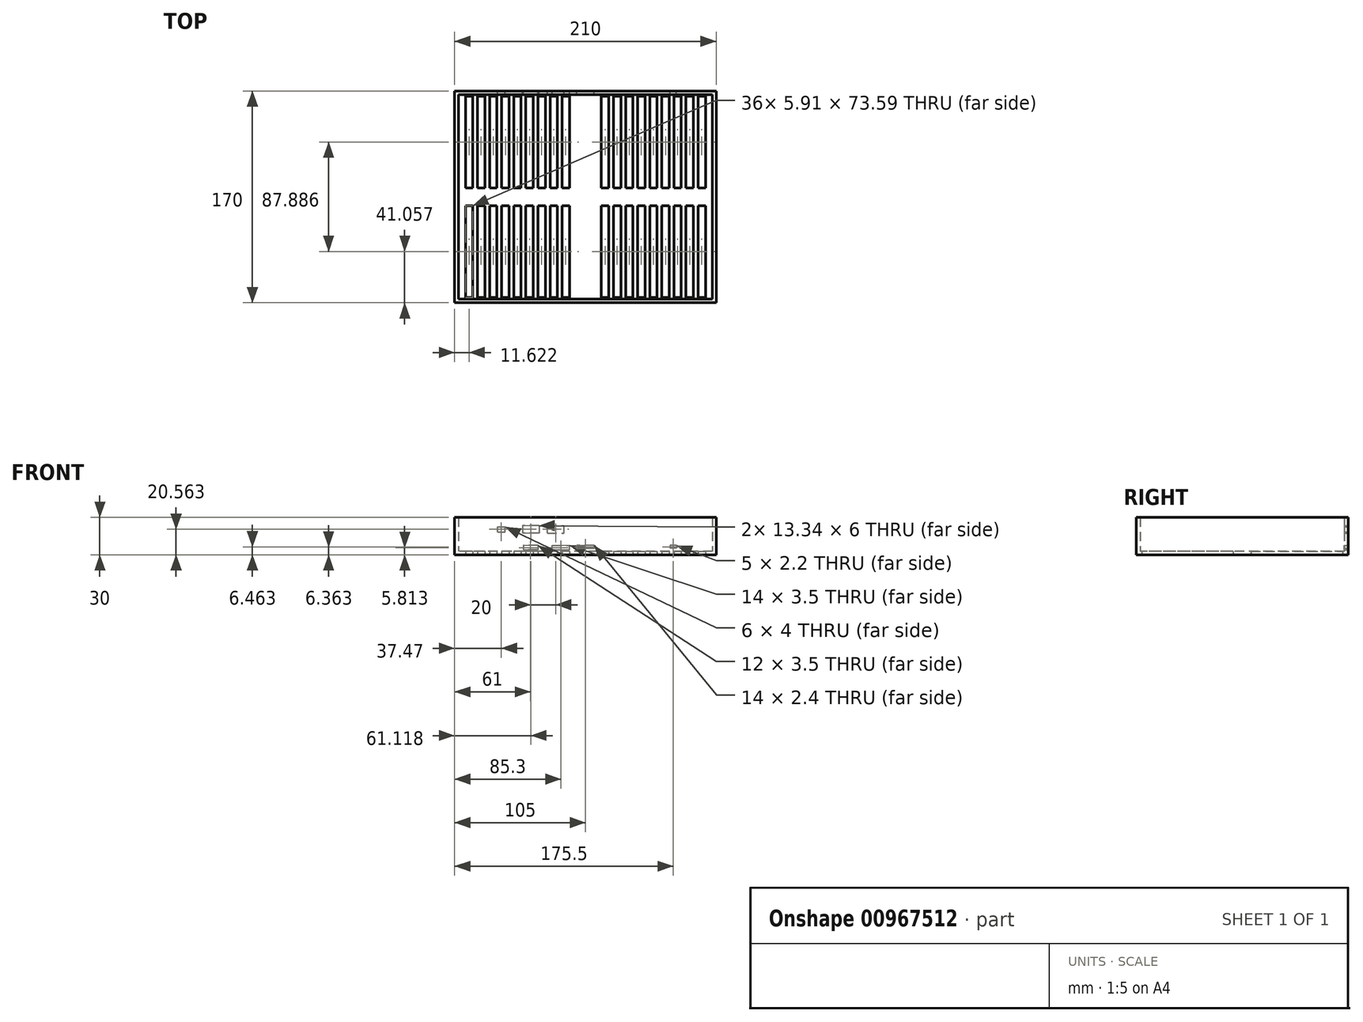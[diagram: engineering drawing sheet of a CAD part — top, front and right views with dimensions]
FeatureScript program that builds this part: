
annotation { "Feature Type Name" : "Feature", "Feature Type Description" : "" }
export const myFeature = defineFeature(function(context is Context, id is Id, definition is map)
    precondition{}
    {
        {
            var Q0;
            Q0=qCreatedBy(makeId("Top.planeOp"),FACE);
            var sketch = newSketch(context, id + "F0", { "sketchPlane" : qUnion([Q0])});
            skLineSegment(sketch, "E0.bottom", {"start": v(105, 85) * mm, "end": v(-105, 85) * mm});
            skLineSegment(sketch, "E0.top", {"start": v(105, -85) * mm, "end": v(-105, -85) * mm});
            skLineSegment(sketch, "E0.left", {"start": v(105, 85) * mm, "end": v(105, -85) * mm});
            skLineSegment(sketch, "E0.right", {"start": v(-105, 85) * mm, "end": v(-105, -85) * mm});
            skPoint(sketch, "E0.middle", {"position": v(0, 0) * mm});
            skSolve(sketch);
        }
        {
            var Q0;
            Q0 = qSketchRegion(id + "F0", true);
            extrude(context, id + "F1", {"entities" : qUnion([Q0]), "depth" : 30 * mm, "offsetDistance" : 25 * mm});
        }
        {
            var Q0;
            Q0=makeQuery(id+"F1.opExtrude","CAP_FACE",FACE,{"disambiguationData":[OSD([sQuery(id+"F0.wireOp",EDGE,"E0.bottom"),sQuery(id+"F0.wireOp",EDGE,"E0.top"),sQuery(id+"F0.wireOp",EDGE,"E0.left"),sQuery(id+"F0.wireOp",EDGE,"E0.right")])],"isStart":false});
            shell(context, id + "F2", {"entities" : qUnion([Q0]), "thickness" : 3 * mm});
        }
        {
            var Q0;
            Q0=makeQuery(id+"F1.opExtrude","SWEPT_FACE",FACE,{"disambiguationData":[OSD([sQuery(id+"F0.wireOp",EDGE,"E0.bottom")])]});
            var sketch = newSketch(context, id + "F3", { "sketchPlane" : qUnion([Q0])});
            skLineSegment(sketch, "E1.bottom", {"start": v(38, 7.56) * mm, "end": v(50, 7.56) * mm});
            skLineSegment(sketch, "E1.top", {"start": v(38, 4.06) * mm, "end": v(50, 4.06) * mm});
            skLineSegment(sketch, "E1.left", {"start": v(38, 7.56) * mm, "end": v(38, 4.06) * mm});
            skLineSegment(sketch, "E1.right", {"start": v(50, 7.56) * mm, "end": v(50, 4.06) * mm});
            skPoint(sketch, "E1.middle", {"position": v(44, 5.81) * mm});
            skLineSegment(sketch, "E2.bottom", {"start": v(26.7, 4.06) * mm, "end": v(12.7, 4.06) * mm});
            skLineSegment(sketch, "E2.top", {"start": v(26.7, 7.56) * mm, "end": v(12.7, 7.56) * mm});
            skLineSegment(sketch, "E2.left", {"start": v(26.7, 4.06) * mm, "end": v(26.7, 7.56) * mm});
            skLineSegment(sketch, "E2.right", {"start": v(12.7, 4.06) * mm, "end": v(12.7, 7.56) * mm});
            skPoint(sketch, "E2.middle", {"position": v(19.7, 5.81) * mm});
            skLineSegment(sketch, "E3.bottom", {"start": v(-7, 7.56) * mm, "end": v(7, 7.56) * mm});
            skLineSegment(sketch, "E3.top", {"start": v(-7, 5.16) * mm, "end": v(7, 5.16) * mm});
            skLineSegment(sketch, "E3.left", {"start": v(-7, 7.56) * mm, "end": v(-7, 5.16) * mm});
            skLineSegment(sketch, "E3.right", {"start": v(7, 7.56) * mm, "end": v(7, 5.16) * mm});
            skPoint(sketch, "E3.middle", {"position": v(0, 6.36) * mm});
            skLineSegment(sketch, "E4.bottom", {"start": v(-73, 7.56) * mm, "end": v(-68, 7.56) * mm});
            skLineSegment(sketch, "E4.top", {"start": v(-73, 5.36) * mm, "end": v(-68, 5.36) * mm});
            skLineSegment(sketch, "E4.left", {"start": v(-73, 7.56) * mm, "end": v(-73, 5.36) * mm});
            skLineSegment(sketch, "E4.right", {"start": v(-68, 7.56) * mm, "end": v(-68, 5.36) * mm});
            skPoint(sketch, "E4.middle", {"position": v(-70.5, 6.46) * mm});
            skLineSegment(sketch, "E5.bottom", {"start": v(37.21, 23.56) * mm, "end": v(50.55, 23.56) * mm});
            skLineSegment(sketch, "E5.top", {"start": v(37.21, 17.56) * mm, "end": v(50.55, 17.56) * mm});
            skLineSegment(sketch, "E5.left", {"start": v(37.21, 23.56) * mm, "end": v(37.21, 17.56) * mm});
            skLineSegment(sketch, "E5.right", {"start": v(50.55, 23.56) * mm, "end": v(50.55, 17.56) * mm});
            skPoint(sketch, "E5.middle", {"position": v(43.88, 20.56) * mm});
            skLineSegment(sketch, "E6.bottom", {"start": v(30.55, 17.56) * mm, "end": v(17.21, 17.56) * mm});
            skLineSegment(sketch, "E6.top", {"start": v(30.55, 23.56) * mm, "end": v(17.21, 23.56) * mm});
            skLineSegment(sketch, "E6.left", {"start": v(30.55, 17.56) * mm, "end": v(30.55, 23.56) * mm});
            skLineSegment(sketch, "E6.right", {"start": v(17.21, 17.56) * mm, "end": v(17.21, 23.56) * mm});
            skPoint(sketch, "E6.middle", {"position": v(23.88, 20.56) * mm});
            skLineSegment(sketch, "E7.bottom", {"start": v(70.53, 18.56) * mm, "end": v(64.53, 18.56) * mm});
            skLineSegment(sketch, "E7.top", {"start": v(70.53, 22.56) * mm, "end": v(64.53, 22.56) * mm});
            skLineSegment(sketch, "E7.left", {"start": v(70.53, 18.56) * mm, "end": v(70.53, 22.56) * mm});
            skLineSegment(sketch, "E7.right", {"start": v(64.53, 18.56) * mm, "end": v(64.53, 22.56) * mm});
            skPoint(sketch, "E7.middle", {"position": v(67.53, 20.56) * mm});
            skPoint(sketch, "E7.middle.positionSnap0", {"position": v(50.55, 20.56) * mm});
            skPoint(sketch, "E7.centerSnap0", {"position": v(50.55, 20.56) * mm});
            skSolve(sketch);
        }
        {
            var Q0;
            Q0 = qSketchRegion(id + "F3", true);
            extrude(context, id + "F4", {"entities" : qUnion([Q0]), "operationType" : NewBodyOperationType.REMOVE, "oppositeDirection" : true, "depth" : 25 * mm, "offsetDistance" : 25 * mm});
        }
        {
            var Q0;
            Q0=makeQuery(id+"F1.opExtrude","CAP_FACE",FACE,{"disambiguationData":[OSD([sQuery(id+"F0.wireOp",EDGE,"E0.bottom"),sQuery(id+"F0.wireOp",EDGE,"E0.top"),sQuery(id+"F0.wireOp",EDGE,"E0.left"),sQuery(id+"F0.wireOp",EDGE,"E0.right")])],"isStart":true});
            var sketch = newSketch(context, id + "F5", { "sketchPlane" : qUnion([Q0])});
            skLineSegment(sketch, "E8", {"start": v(0, 85) * mm, "end": v(0, -85) * mm});
            skLineSegment(sketch, "E9.bottom", {"start": v(-96.33, 80.74) * mm, "end": v(-90.42, 80.74) * mm});
            skLineSegment(sketch, "E9.top", {"start": v(-96.33, 7.15) * mm, "end": v(-90.42, 7.15) * mm});
            skLineSegment(sketch, "E9.left", {"start": v(-96.33, 80.74) * mm, "end": v(-96.33, 7.15) * mm});
            skLineSegment(sketch, "E9.right", {"start": v(-90.42, 80.74) * mm, "end": v(-90.42, 7.15) * mm});
            skLineSegment(sketch, "E10.MirrorCS", {"start": v(-90.42, -80.74) * mm, "end": v(-90.42, -7.15) * mm});
            skLineSegment(sketch, "E11.MirrorCS", {"start": v(-96.33, -80.74) * mm, "end": v(-96.33, -7.15) * mm});
            skLineSegment(sketch, "E12.MirrorCS", {"start": v(-96.33, -80.74) * mm, "end": v(-90.42, -80.74) * mm});
            skLineSegment(sketch, "E13.MirrorCS", {"start": v(-96.33, -7.15) * mm, "end": v(-90.42, -7.15) * mm});
            skLineSegment(sketch, "E14.1.0.0", {"start": v(-86.63, 80.74) * mm, "end": v(-86.63, 7.15) * mm});
            skLineSegment(sketch, "E14.1.0.1", {"start": v(-80.72, 80.74) * mm, "end": v(-80.72, 7.15) * mm});
            skLineSegment(sketch, "E14.1.0.2", {"start": v(-86.63, 80.74) * mm, "end": v(-80.72, 80.74) * mm});
            skLineSegment(sketch, "E14.1.0.3", {"start": v(-86.63, 7.15) * mm, "end": v(-80.72, 7.15) * mm});
            skLineSegment(sketch, "E14.1.0.4", {"start": v(-86.63, -7.15) * mm, "end": v(-80.72, -7.15) * mm});
            skLineSegment(sketch, "E14.1.0.5", {"start": v(-86.63, -80.74) * mm, "end": v(-86.63, -7.15) * mm});
            skLineSegment(sketch, "E14.1.0.6", {"start": v(-80.72, -80.74) * mm, "end": v(-80.72, -7.15) * mm});
            skLineSegment(sketch, "E14.1.0.7", {"start": v(-86.63, -80.74) * mm, "end": v(-80.72, -80.74) * mm});
            skLineSegment(sketch, "E14.2.0.0", {"start": v(-76.93, 80.74) * mm, "end": v(-76.93, 7.15) * mm});
            skLineSegment(sketch, "E14.2.0.1", {"start": v(-71.02, 80.74) * mm, "end": v(-71.02, 7.15) * mm});
            skLineSegment(sketch, "E14.2.0.2", {"start": v(-76.93, 80.74) * mm, "end": v(-71.02, 80.74) * mm});
            skLineSegment(sketch, "E14.2.0.3", {"start": v(-76.93, 7.15) * mm, "end": v(-71.02, 7.15) * mm});
            skLineSegment(sketch, "E14.2.0.4", {"start": v(-76.93, -7.15) * mm, "end": v(-71.02, -7.15) * mm});
            skLineSegment(sketch, "E14.2.0.5", {"start": v(-76.93, -80.74) * mm, "end": v(-76.93, -7.15) * mm});
            skLineSegment(sketch, "E14.2.0.6", {"start": v(-71.02, -80.74) * mm, "end": v(-71.02, -7.15) * mm});
            skLineSegment(sketch, "E14.2.0.7", {"start": v(-76.93, -80.74) * mm, "end": v(-71.02, -80.74) * mm});
            skLineSegment(sketch, "E15.0.3.0", {"start": v(-67.23, 80.74) * mm, "end": v(-67.23, 7.15) * mm});
            skLineSegment(sketch, "E15.3.3.0", {"start": v(-61.32, 80.74) * mm, "end": v(-61.32, 7.15) * mm});
            skLineSegment(sketch, "E15.6.3.0", {"start": v(-67.23, 80.74) * mm, "end": v(-61.32, 80.74) * mm});
            skLineSegment(sketch, "E15.9.3.0", {"start": v(-67.23, 7.15) * mm, "end": v(-61.32, 7.15) * mm});
            skLineSegment(sketch, "E15.12.3.0", {"start": v(-67.23, -7.15) * mm, "end": v(-61.32, -7.15) * mm});
            skLineSegment(sketch, "E15.15.3.0", {"start": v(-67.23, -80.74) * mm, "end": v(-67.23, -7.15) * mm});
            skLineSegment(sketch, "E15.18.3.0", {"start": v(-61.32, -80.74) * mm, "end": v(-61.32, -7.15) * mm});
            skLineSegment(sketch, "E15.21.3.0", {"start": v(-67.23, -80.74) * mm, "end": v(-61.32, -80.74) * mm});
            skLineSegment(sketch, "E15.0.4.0", {"start": v(-57.53, 80.74) * mm, "end": v(-57.53, 7.15) * mm});
            skLineSegment(sketch, "E15.3.4.0", {"start": v(-51.62, 80.74) * mm, "end": v(-51.62, 7.15) * mm});
            skLineSegment(sketch, "E15.6.4.0", {"start": v(-57.53, 80.74) * mm, "end": v(-51.62, 80.74) * mm});
            skLineSegment(sketch, "E15.9.4.0", {"start": v(-57.53, 7.15) * mm, "end": v(-51.62, 7.15) * mm});
            skLineSegment(sketch, "E15.12.4.0", {"start": v(-57.53, -7.15) * mm, "end": v(-51.62, -7.15) * mm});
            skLineSegment(sketch, "E15.15.4.0", {"start": v(-57.53, -80.74) * mm, "end": v(-57.53, -7.15) * mm});
            skLineSegment(sketch, "E15.18.4.0", {"start": v(-51.62, -80.74) * mm, "end": v(-51.62, -7.15) * mm});
            skLineSegment(sketch, "E15.21.4.0", {"start": v(-57.53, -80.74) * mm, "end": v(-51.62, -80.74) * mm});
            skLineSegment(sketch, "E16.0.5.0", {"start": v(-47.83, 80.74) * mm, "end": v(-47.83, 7.15) * mm});
            skLineSegment(sketch, "E16.3.5.0", {"start": v(-41.92, 80.74) * mm, "end": v(-41.92, 7.15) * mm});
            skLineSegment(sketch, "E16.6.5.0", {"start": v(-47.83, 80.74) * mm, "end": v(-41.92, 80.74) * mm});
            skLineSegment(sketch, "E16.9.5.0", {"start": v(-47.83, 7.15) * mm, "end": v(-41.92, 7.15) * mm});
            skLineSegment(sketch, "E16.12.5.0", {"start": v(-47.83, -7.15) * mm, "end": v(-41.92, -7.15) * mm});
            skLineSegment(sketch, "E16.15.5.0", {"start": v(-47.83, -80.74) * mm, "end": v(-47.83, -7.15) * mm});
            skLineSegment(sketch, "E16.18.5.0", {"start": v(-41.92, -80.74) * mm, "end": v(-41.92, -7.15) * mm});
            skLineSegment(sketch, "E16.21.5.0", {"start": v(-47.83, -80.74) * mm, "end": v(-41.92, -80.74) * mm});
            skLineSegment(sketch, "E16.0.6.0", {"start": v(-38.13, 80.74) * mm, "end": v(-38.13, 7.15) * mm});
            skLineSegment(sketch, "E16.3.6.0", {"start": v(-32.22, 80.74) * mm, "end": v(-32.22, 7.15) * mm});
            skLineSegment(sketch, "E16.6.6.0", {"start": v(-38.13, 80.74) * mm, "end": v(-32.22, 80.74) * mm});
            skLineSegment(sketch, "E16.9.6.0", {"start": v(-38.13, 7.15) * mm, "end": v(-32.22, 7.15) * mm});
            skLineSegment(sketch, "E16.12.6.0", {"start": v(-38.13, -7.15) * mm, "end": v(-32.22, -7.15) * mm});
            skLineSegment(sketch, "E16.15.6.0", {"start": v(-38.13, -80.74) * mm, "end": v(-38.13, -7.15) * mm});
            skLineSegment(sketch, "E16.18.6.0", {"start": v(-32.22, -80.74) * mm, "end": v(-32.22, -7.15) * mm});
            skLineSegment(sketch, "E16.21.6.0", {"start": v(-38.13, -80.74) * mm, "end": v(-32.22, -80.74) * mm});
            skLineSegment(sketch, "E17.0.7.0", {"start": v(-28.43, 80.74) * mm, "end": v(-28.43, 7.15) * mm});
            skLineSegment(sketch, "E17.3.7.0", {"start": v(-22.52, 80.74) * mm, "end": v(-22.52, 7.15) * mm});
            skLineSegment(sketch, "E17.6.7.0", {"start": v(-28.43, 80.74) * mm, "end": v(-22.52, 80.74) * mm});
            skLineSegment(sketch, "E17.9.7.0", {"start": v(-28.43, 7.15) * mm, "end": v(-22.52, 7.15) * mm});
            skLineSegment(sketch, "E17.12.7.0", {"start": v(-28.43, -7.15) * mm, "end": v(-22.52, -7.15) * mm});
            skLineSegment(sketch, "E17.15.7.0", {"start": v(-28.43, -80.74) * mm, "end": v(-28.43, -7.15) * mm});
            skLineSegment(sketch, "E17.18.7.0", {"start": v(-22.52, -80.74) * mm, "end": v(-22.52, -7.15) * mm});
            skLineSegment(sketch, "E17.21.7.0", {"start": v(-28.43, -80.74) * mm, "end": v(-22.52, -80.74) * mm});
            skLineSegment(sketch, "E17.0.8.0", {"start": v(-18.73, 80.74) * mm, "end": v(-18.73, 7.15) * mm});
            skLineSegment(sketch, "E17.3.8.0", {"start": v(-12.82, 80.74) * mm, "end": v(-12.82, 7.15) * mm});
            skLineSegment(sketch, "E17.6.8.0", {"start": v(-18.73, 80.74) * mm, "end": v(-12.82, 80.74) * mm});
            skLineSegment(sketch, "E17.9.8.0", {"start": v(-18.73, 7.15) * mm, "end": v(-12.82, 7.15) * mm});
            skLineSegment(sketch, "E17.12.8.0", {"start": v(-18.73, -7.15) * mm, "end": v(-12.82, -7.15) * mm});
            skLineSegment(sketch, "E17.15.8.0", {"start": v(-18.73, -80.74) * mm, "end": v(-18.73, -7.15) * mm});
            skLineSegment(sketch, "E17.18.8.0", {"start": v(-12.82, -80.74) * mm, "end": v(-12.82, -7.15) * mm});
            skLineSegment(sketch, "E17.21.8.0", {"start": v(-18.73, -80.74) * mm, "end": v(-12.82, -80.74) * mm});
            skLineSegment(sketch, "E18.MirrorCS", {"start": v(96.33, 80.74) * mm, "end": v(96.33, 7.15) * mm});
            skLineSegment(sketch, "E19.MirrorCS", {"start": v(90.42, 80.74) * mm, "end": v(90.42, 7.15) * mm});
            skLineSegment(sketch, "E20.MirrorCS", {"start": v(86.63, 80.74) * mm, "end": v(86.63, 7.15) * mm});
            skLineSegment(sketch, "E21.MirrorCS", {"start": v(80.72, 80.74) * mm, "end": v(80.72, 7.15) * mm});
            skLineSegment(sketch, "E22.MirrorCS", {"start": v(76.93, 80.74) * mm, "end": v(76.93, 7.15) * mm});
            skLineSegment(sketch, "E23.MirrorCS", {"start": v(71.02, 80.74) * mm, "end": v(71.02, 7.15) * mm});
            skLineSegment(sketch, "E24.MirrorCS", {"start": v(67.23, 80.74) * mm, "end": v(67.23, 7.15) * mm});
            skLineSegment(sketch, "E25.MirrorCS", {"start": v(61.32, 80.74) * mm, "end": v(61.32, 7.15) * mm});
            skLineSegment(sketch, "E26.MirrorCS", {"start": v(57.53, 80.74) * mm, "end": v(57.53, 7.15) * mm});
            skLineSegment(sketch, "E27.MirrorCS", {"start": v(51.62, 80.74) * mm, "end": v(51.62, 7.15) * mm});
            skLineSegment(sketch, "E28.MirrorCS", {"start": v(47.83, 80.74) * mm, "end": v(47.83, 7.15) * mm});
            skLineSegment(sketch, "E29.MirrorCS", {"start": v(41.92, 80.74) * mm, "end": v(41.92, 7.15) * mm});
            skLineSegment(sketch, "E30.MirrorCS", {"start": v(38.13, 80.74) * mm, "end": v(38.13, 7.15) * mm});
            skLineSegment(sketch, "E31.MirrorCS", {"start": v(32.22, 80.74) * mm, "end": v(32.22, 7.15) * mm});
            skLineSegment(sketch, "E32.MirrorCS", {"start": v(28.43, 80.74) * mm, "end": v(28.43, 7.15) * mm});
            skLineSegment(sketch, "E33.MirrorCS", {"start": v(22.52, 80.74) * mm, "end": v(22.52, 7.15) * mm});
            skLineSegment(sketch, "E34.MirrorCS", {"start": v(18.73, 80.74) * mm, "end": v(18.73, 7.15) * mm});
            skLineSegment(sketch, "E35.MirrorCS", {"start": v(12.82, 80.74) * mm, "end": v(12.82, 7.15) * mm});
            skLineSegment(sketch, "E36.MirrorCS", {"start": v(96.33, 80.74) * mm, "end": v(90.42, 80.74) * mm});
            skLineSegment(sketch, "E37.MirrorCS", {"start": v(86.63, 80.74) * mm, "end": v(80.72, 80.74) * mm});
            skLineSegment(sketch, "E38.MirrorCS", {"start": v(76.93, 80.74) * mm, "end": v(71.02, 80.74) * mm});
            skLineSegment(sketch, "E39.MirrorCS", {"start": v(67.23, 80.74) * mm, "end": v(61.32, 80.74) * mm});
            skLineSegment(sketch, "E40.MirrorCS", {"start": v(57.53, 80.74) * mm, "end": v(51.62, 80.74) * mm});
            skLineSegment(sketch, "E41.MirrorCS", {"start": v(47.83, 80.74) * mm, "end": v(41.92, 80.74) * mm});
            skLineSegment(sketch, "E42.MirrorCS", {"start": v(38.13, 80.74) * mm, "end": v(32.22, 80.74) * mm});
            skLineSegment(sketch, "E43.MirrorCS", {"start": v(28.43, 80.74) * mm, "end": v(22.52, 80.74) * mm});
            skLineSegment(sketch, "E44.MirrorCS", {"start": v(18.73, 80.74) * mm, "end": v(12.82, 80.74) * mm});
            skLineSegment(sketch, "E45.MirrorCS", {"start": v(86.63, 7.15) * mm, "end": v(80.72, 7.15) * mm});
            skLineSegment(sketch, "E46.MirrorCS", {"start": v(76.93, 7.15) * mm, "end": v(71.02, 7.15) * mm});
            skLineSegment(sketch, "E47.MirrorCS", {"start": v(67.23, 7.15) * mm, "end": v(61.32, 7.15) * mm});
            skLineSegment(sketch, "E48.MirrorCS", {"start": v(57.53, 7.15) * mm, "end": v(51.62, 7.15) * mm});
            skLineSegment(sketch, "E49.MirrorCS", {"start": v(47.83, 7.15) * mm, "end": v(41.92, 7.15) * mm});
            skLineSegment(sketch, "E50.MirrorCS", {"start": v(38.13, 7.15) * mm, "end": v(32.22, 7.15) * mm});
            skLineSegment(sketch, "E51.MirrorCS", {"start": v(28.43, 7.15) * mm, "end": v(22.52, 7.15) * mm});
            skLineSegment(sketch, "E52.MirrorCS", {"start": v(18.73, 7.15) * mm, "end": v(12.82, 7.15) * mm});
            skLineSegment(sketch, "E53.MirrorCS", {"start": v(96.33, 7.15) * mm, "end": v(90.42, 7.15) * mm});
            skLineSegment(sketch, "E54.MirrorCS", {"start": v(96.33, -80.74) * mm, "end": v(96.33, -7.15) * mm});
            skLineSegment(sketch, "E55.MirrorCS", {"start": v(90.42, -80.74) * mm, "end": v(90.42, -7.15) * mm});
            skLineSegment(sketch, "E56.MirrorCS", {"start": v(80.72, -80.74) * mm, "end": v(80.72, -7.15) * mm});
            skLineSegment(sketch, "E57.MirrorCS", {"start": v(76.93, -80.74) * mm, "end": v(76.93, -7.15) * mm});
            skLineSegment(sketch, "E58.MirrorCS", {"start": v(71.02, -80.74) * mm, "end": v(71.02, -7.15) * mm});
            skLineSegment(sketch, "E59.MirrorCS", {"start": v(67.23, -80.74) * mm, "end": v(67.23, -7.15) * mm});
            skLineSegment(sketch, "E60.MirrorCS", {"start": v(61.32, -80.74) * mm, "end": v(61.32, -7.15) * mm});
            skLineSegment(sketch, "E61.MirrorCS", {"start": v(57.53, -80.74) * mm, "end": v(57.53, -7.15) * mm});
            skLineSegment(sketch, "E62.MirrorCS", {"start": v(51.62, -80.74) * mm, "end": v(51.62, -7.15) * mm});
            skLineSegment(sketch, "E63.MirrorCS", {"start": v(47.83, -80.74) * mm, "end": v(47.83, -7.15) * mm});
            skLineSegment(sketch, "E64.MirrorCS", {"start": v(41.92, -80.74) * mm, "end": v(41.92, -7.15) * mm});
            skLineSegment(sketch, "E65.MirrorCS", {"start": v(38.13, -80.74) * mm, "end": v(38.13, -7.15) * mm});
            skLineSegment(sketch, "E66.MirrorCS", {"start": v(32.22, -80.74) * mm, "end": v(32.22, -7.15) * mm});
            skLineSegment(sketch, "E67.MirrorCS", {"start": v(28.43, -80.74) * mm, "end": v(28.43, -7.15) * mm});
            skLineSegment(sketch, "E68.MirrorCS", {"start": v(22.52, -80.74) * mm, "end": v(22.52, -7.15) * mm});
            skLineSegment(sketch, "E69.MirrorCS", {"start": v(18.73, -80.74) * mm, "end": v(18.73, -7.15) * mm});
            skLineSegment(sketch, "E70.MirrorCS", {"start": v(12.82, -80.74) * mm, "end": v(12.82, -7.15) * mm});
            skLineSegment(sketch, "E71.MirrorCS", {"start": v(96.33, -7.15) * mm, "end": v(90.42, -7.15) * mm});
            skLineSegment(sketch, "E72.MirrorCS", {"start": v(86.63, -7.15) * mm, "end": v(80.72, -7.15) * mm});
            skLineSegment(sketch, "E73.MirrorCS", {"start": v(76.93, -7.15) * mm, "end": v(71.02, -7.15) * mm});
            skLineSegment(sketch, "E74.MirrorCS", {"start": v(67.23, -7.15) * mm, "end": v(61.32, -7.15) * mm});
            skLineSegment(sketch, "E75.MirrorCS", {"start": v(57.53, -7.15) * mm, "end": v(51.62, -7.15) * mm});
            skLineSegment(sketch, "E76.MirrorCS", {"start": v(47.83, -7.15) * mm, "end": v(41.92, -7.15) * mm});
            skLineSegment(sketch, "E77.MirrorCS", {"start": v(38.13, -7.15) * mm, "end": v(32.22, -7.15) * mm});
            skLineSegment(sketch, "E78.MirrorCS", {"start": v(28.43, -7.15) * mm, "end": v(22.52, -7.15) * mm});
            skLineSegment(sketch, "E79.MirrorCS", {"start": v(18.73, -7.15) * mm, "end": v(12.82, -7.15) * mm});
            skLineSegment(sketch, "E80.MirrorCS", {"start": v(96.33, -80.74) * mm, "end": v(90.42, -80.74) * mm});
            skLineSegment(sketch, "E81.MirrorCS", {"start": v(86.63, -80.74) * mm, "end": v(80.72, -80.74) * mm});
            skLineSegment(sketch, "E82.MirrorCS", {"start": v(76.93, -80.74) * mm, "end": v(71.02, -80.74) * mm});
            skLineSegment(sketch, "E83.MirrorCS", {"start": v(67.23, -80.74) * mm, "end": v(61.32, -80.74) * mm});
            skLineSegment(sketch, "E84.MirrorCS", {"start": v(57.53, -80.74) * mm, "end": v(51.62, -80.74) * mm});
            skLineSegment(sketch, "E85.MirrorCS", {"start": v(47.83, -80.74) * mm, "end": v(41.92, -80.74) * mm});
            skLineSegment(sketch, "E86.MirrorCS", {"start": v(38.13, -80.74) * mm, "end": v(32.22, -80.74) * mm});
            skLineSegment(sketch, "E87.MirrorCS", {"start": v(28.43, -80.74) * mm, "end": v(22.52, -80.74) * mm});
            skLineSegment(sketch, "E88.MirrorCS", {"start": v(18.73, -80.74) * mm, "end": v(12.82, -80.74) * mm});
            skLineSegment(sketch, "E89.MirrorCS", {"start": v(86.63, -80.74) * mm, "end": v(86.63, -7.15) * mm});
            skSolve(sketch);
        }
        {
            var Q0;
            Q0 = qSketchRegion(id + "F5", true);
            extrude(context, id + "F6", {"entities" : qUnion([Q0]), "operationType" : NewBodyOperationType.REMOVE, "oppositeDirection" : true, "depth" : 25 * mm, "offsetDistance" : 25 * mm});
        }
    });
